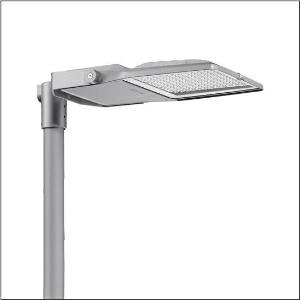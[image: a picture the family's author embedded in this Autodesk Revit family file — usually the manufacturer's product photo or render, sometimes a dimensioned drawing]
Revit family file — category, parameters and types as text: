
# Revit family: floodlight_fl_21_iq_midi___pl61_5xa7781e2c3a_352e
name_source: partatom
category: Lighting Fixtures
units: mm (PartAtom-declared; Revit-internal decimal feet)

## family parameters
Cut with Voids When Loaded = No
Host = Face
Light Source = No
Part Type = Normal
Room Calculation Point = No
Round Connector Dimension = Use Diameter
Shared = No

## types (1)
- --- (1 x LED, 26360 lm, 208.1 W, 3000K)
    Apparent Load = 208 VA
    CIE Flux Codes = 33 65 98 100 100
    Color Rendering = 70
    Color Temperature = 3000K
    Default Elevation = 1800 mm
    Description = Floodlight FL 21 iQ midi, floodlight, primary light control with lens, of PMMA, primary optical cover: protective disc, of toughened safety glass, transparent, light distribution: PL61, light emission: direct distribution, installation type: surface-mounted, LED, High Power LED, rated luminous flux: 26.360lm, luminous efficacy: 127lm/W, light colour: 730, colour temperature: 3000K, control gear: ECG iQ, control: optimised constant luminous flux control (CLO 2.0), Desk-Remote (wireless, voltage-free reading and setting of iQ features in the workshop via application-optimized NFC function/RFID function), Light-Fading, Smart-Wire, Night-Set, Lumen-Switch, Temp-Guard, Auto-Match, with terminal, 6-pole, mains connection: 220..240V, AC, 50/60Hz, start of lifetime: 208W, end of service life: 227W, reduction: 90W, luminaire housing, of diecast aluminium, powder-coated, Siteco® metallic grey (DB 702S), corrosivity category C5 mid according to DIN EN ISO 12944, sealing non-destructively replaceable, please order mast flange separately, mast bracket, of steel, galvanised, powder-coated, Siteco® metallic grey (DB 702S), protection rating (complete): IP66, insulation class (complete): insulation class II (safety insulation), certification: CE, protection symbol: D, impact resistance: IK08, permissible operating ambient temperature: -40..+40°C, permissible operating ambient temperature for outdoor applications: -40..+50°C, standard: DIN EN 12944, LABS conformity tested according to VDMA 24364:2018-05, packaging unit: 1 piece

Light Distribution: PL61
    Height = 76 mm
    Lamp = 1 x LED
    Lamp Light Flux = 26360 lm
    Lamp Power = 208.1 W
    Lamp count = 1
    Length = 657 mm
    Luminous efficacy = 127 lm/W
    Manufacturer = Siteco
    ModVariant = No
    Model = 5XA7781E2C3A
    Number of Poles = 1
    OnlyDefault = Yes
    Power Factor = 1
    Product Name = Floodlight FL 21 iQ midi | PL61
    Product group = floodlight | pylon annexe
    ProductGroupID = 6200
    Protection Class = Protection class II
    Protection Degree = IP 66
    RLX_Detail_Level = 1
    RLX_Emergency_Light_Flux = 0 lm
    RLX_Emergency_Type = 0
    RLX_Emergency_Type_DB = No
    RlxData = <blob elided: 153553 chars, md5=0ab83d8c>
    Socket = socket
    Standby Power = 0 W
    System Light Flux = 26360 lm
    System Power = 208 W
    Type Comments = factory setting: luminous flux: 100 % | dim-lin: 254 | 710 mA
    Type Image = l_1007123.jpg
    URL = http://relux.com
    VarID = @adj_039065
    Voltage = 0 V
    Weight = 0.00 kg
    Width = 442 mm

## geometry (parser evidence)
native form markers: Blend x4, Sweep x14
no freeform markers — native parametric forms only
